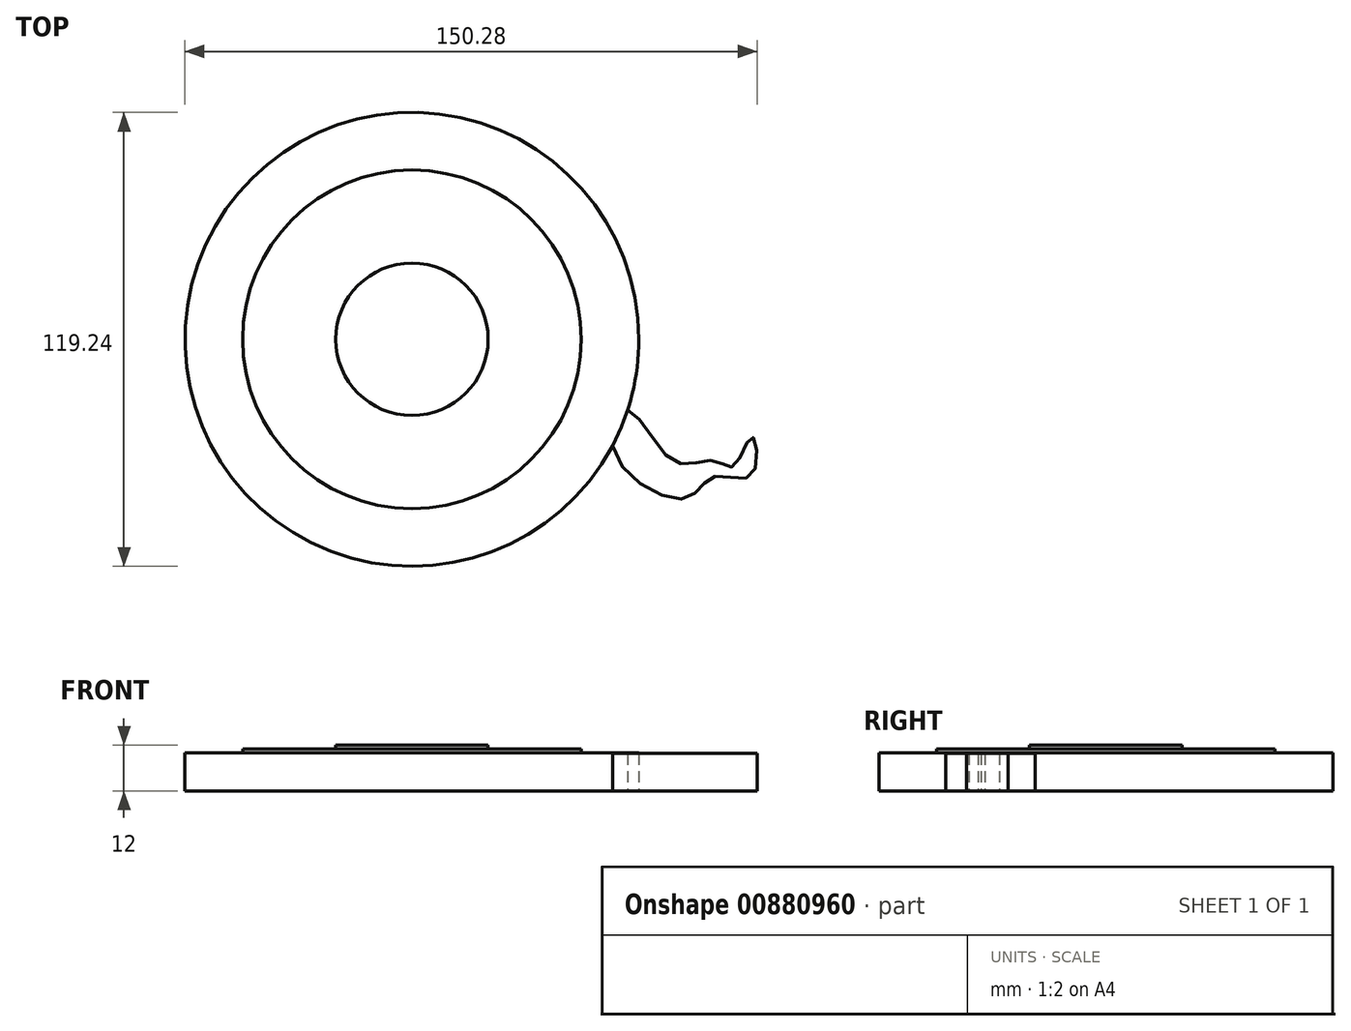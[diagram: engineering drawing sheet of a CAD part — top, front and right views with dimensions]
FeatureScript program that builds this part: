
annotation { "Feature Type Name" : "Feature", "Feature Type Description" : "" }
export const myFeature = defineFeature(function(context is Context, id is Id, definition is map)
    precondition{}
    {
        {
            var Q0;
            Q0=qCreatedBy(makeId("Top.planeOp"),FACE);
            var sketch = newSketch(context, id + "F0", { "sketchPlane" : qUnion([Q0])});
            skCircle(sketch, "E0", {"center": v(0, 0) * mm, "radius": 59.62 * mm});
            skSolve(sketch);
        }
        {
            var Q0;
            Q0=makeQuery(id+"F0.imprint","IMPRINT",FACE,{"disambiguationData":[TD([[makeQuery(id+"F0.imprint","IMPRINT",EDGE,{"derivedFrom":sQuery(id+"F0.wireOp",EDGE,"E0")}),1.0]])]});
            extrude(context, id + "F1", {"entities" : qUnion([Q0]), "depth" : 10 * mm, "offsetDistance" : 25 * mm});
        }
        {
            var Q0;
            Q0=qCreatedBy(makeId("Top.planeOp"),FACE);
            var sketch = newSketch(context, id + "F2", { "sketchPlane" : qUnion([Q0])});
            skFitSpline(sketch, "E1", {"points": [v(56.51, -18.55) * mm, v(68.98, -32.15) * mm, v(79.46, -31.87) * mm, v(84.56, -33.28) * mm, v(89.37, -25.64) * mm, v(89.37, -35.55) * mm, v(79.17, -36.12) * mm, v(72.1, -41.78) * mm, v(53.11, -29.6) * mm, v(56.51, -18.55) * mm]});
            skSolve(sketch);
        }
        {
            var Q0;
            Q0=makeQuery(id+"F2.imprint","IMPRINT",FACE,{"disambiguationData":[TD([[makeQuery(id+"F2.imprint","IMPRINT",EDGE,{"derivedFrom":sQuery(id+"F2.wireOp",EDGE,"E1")}),-1.0]])]});
            extrude(context, id + "F3", {"entities" : qUnion([Q0]), "operationType" : NewBodyOperationType.ADD, "depth" : 9.8 * mm, "offsetDistance" : 25 * mm});
        }
        {
            var Q0;
            Q0=makeQuery(id+"F1.opExtrude","CAP_FACE",FACE,{"disambiguationData":[OSD([sQuery(id+"F0.wireOp",EDGE,"E0")])],"isStart":false});
            var sketch = newSketch(context, id + "F4", { "sketchPlane" : qUnion([Q0])});
            skCircle(sketch, "E2", {"center": v(0, 0) * mm, "radius": 44.47 * mm});
            skSolve(sketch);
        }
        {
            var Q0;
            Q0 = qSketchRegion(id + "F4", true);
            extrude(context, id + "F5", {"entities" : qUnion([Q0]), "operationType" : NewBodyOperationType.ADD, "depth" : 1 * mm, "offsetDistance" : 25 * mm});
        }
        {
            var Q0;
            Q0=makeQuery(id+"F5.opExtrude","CAP_FACE",FACE,{"disambiguationData":[OSD([sQuery(id+"F4.wireOp",EDGE,"E2")])],"isStart":false});
            var sketch = newSketch(context, id + "F6", { "sketchPlane" : qUnion([Q0])});
            skCircle(sketch, "E3", {"center": v(0, 0) * mm, "radius": 20.02 * mm});
            skSolve(sketch);
        }
        {
            var Q0;
            Q0 = qSketchRegion(id + "F6", true);
            extrude(context, id + "F7", {"entities" : qUnion([Q0]), "operationType" : NewBodyOperationType.ADD, "depth" : 1 * mm, "offsetDistance" : 25 * mm});
        }
    });
